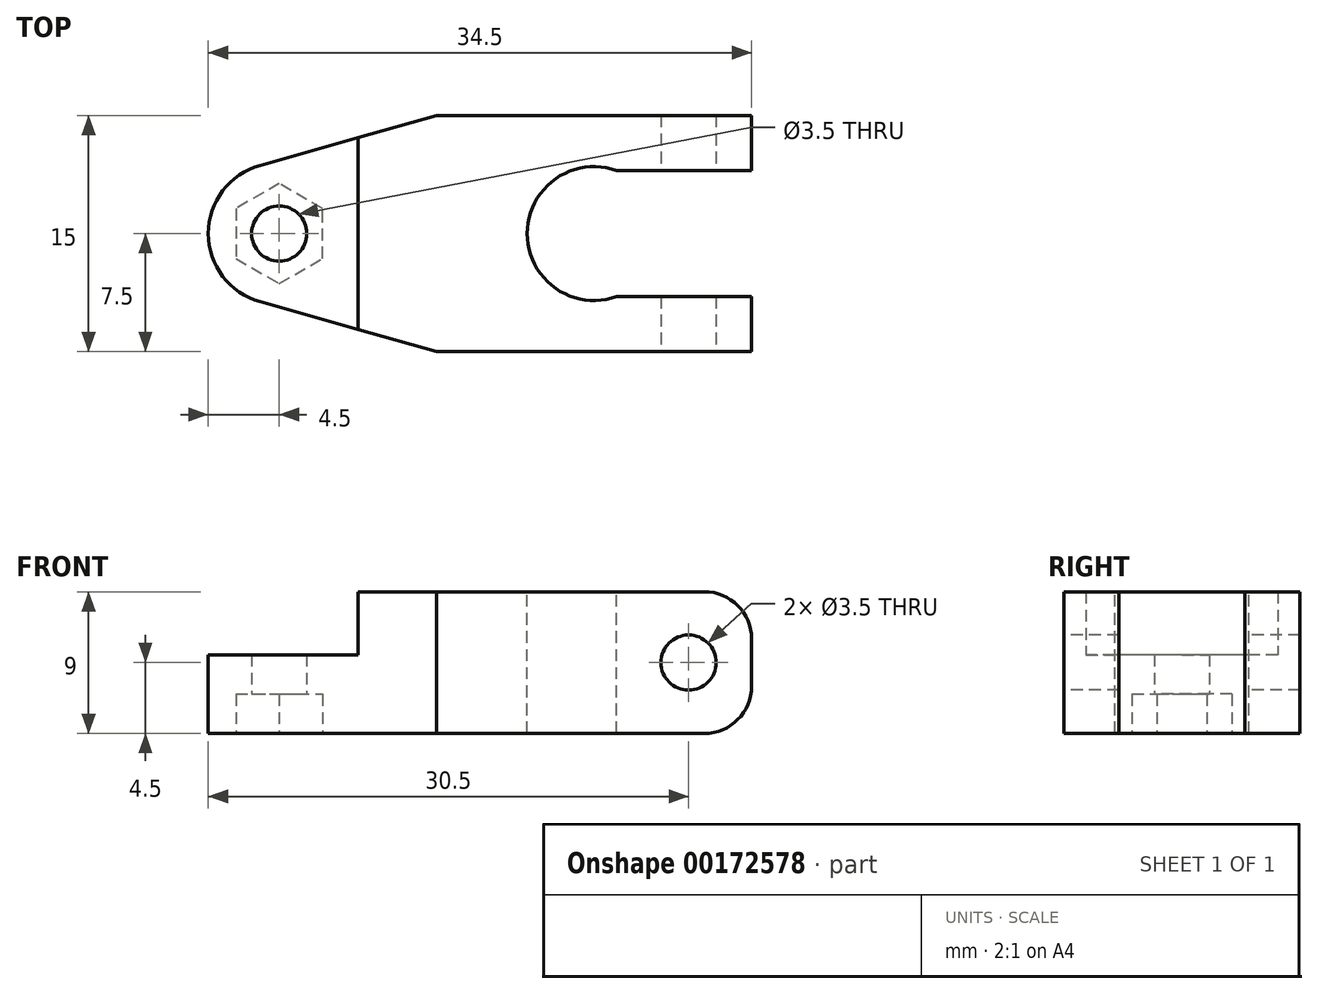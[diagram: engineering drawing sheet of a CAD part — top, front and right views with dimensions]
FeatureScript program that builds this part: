
annotation { "Feature Type Name" : "Feature", "Feature Type Description" : "" }
export const myFeature = defineFeature(function(context is Context, id is Id, definition is map)
    precondition{}
    {
        {
            var Q0;
            Q0=qCreatedBy(makeId("Top.planeOp"),FACE);
            var sketch = newSketch(context, id + "F0", { "sketchPlane" : qUnion([Q0])});
            skCircle(sketch, "E0", {"center": v(0, 0) * mm, "radius": 4.5 * mm});
            skCircle(sketch, "E1", {"center": v(0, 0) * mm, "radius": 1.75 * mm});
            skLineSegment(sketch, "E2.bottom", {"start": v(30, 7.5) * mm, "end": v(10, 7.5) * mm});
            skLineSegment(sketch, "E2.top", {"start": v(30, -7.5) * mm, "end": v(10, -7.5) * mm});
            skLineSegment(sketch, "E2.left", {"start": v(30, 7.5) * mm, "end": v(30, -7.5) * mm});
            skLineSegment(sketch, "E2.right", {"start": v(10, 7.5) * mm, "end": v(10, -7.5) * mm});
            skLineSegment(sketch, "E3", {"start": v(10, 7.5) * mm, "end": v(-1.22, 4.33) * mm});
            skLineSegment(sketch, "E4", {"start": v(10, -7.5) * mm, "end": v(-1.22, -4.33) * mm});
            skSolve(sketch);
        }
        {
            var Q0;
            Q0 = qSketchRegion(id + "F0", true);
            extrude(context, id + "F1", {"entities" : qUnion([Q0]), "depth" : 9 * mm, "offsetDistance" : 25 * mm});
        }
        {
            var Q0;
            Q0=makeQuery(id+"F1.opExtrude","CAP_FACE",FACE,{"disambiguationData":[OSD([sQuery(id+"F0.wireOp",EDGE,"E0"),sQuery(id+"F0.wireOp",EDGE,"M1rwKN8y-CayM-5D3e-yUcK-hpkHA81qaYvP.bottom"),sQuery(id+"F0.wireOp",EDGE,"M1rwKN8y-CayM-5D3e-yUcK-hpkHA81qaYvP.top"),sQuery(id+"F0.wireOp",EDGE,"M1rwKN8y-CayM-5D3e-yUcK-hpkHA81qaYvP.right"),sQuery(id+"F0.wireOp",EDGE,"E1")])],"isStart":false});
            var sketch = newSketch(context, id + "F2", { "sketchPlane" : qUnion([Q0])});
            skLineSegment(sketch, "E5.bottom", {"start": v(-7.93, 7.15) * mm, "end": v(5, 7.15) * mm});
            skLineSegment(sketch, "E5.top", {"start": v(-7.93, -8.4) * mm, "end": v(5, -8.4) * mm});
            skLineSegment(sketch, "E5.left", {"start": v(-7.93, 7.15) * mm, "end": v(-7.93, -8.4) * mm});
            skLineSegment(sketch, "E5.right", {"start": v(5, 7.15) * mm, "end": v(5, -8.4) * mm});
            skSolve(sketch);
        }
        {
            var Q0;
            Q0 = qSketchRegion(id + "F2", true);
            extrude(context, id + "F3", {"entities" : qUnion([Q0]), "operationType" : NewBodyOperationType.REMOVE, "oppositeDirection" : true, "depth" : 4 * mm, "offsetDistance" : 25 * mm});
        }
        {
            var Q0;
            Q0=makeQuery(id+"F1.opExtrude","CAP_FACE",FACE,{"disambiguationData":[OSD([sQuery(id+"F0.wireOp",EDGE,"E0"),sQuery(id+"F0.wireOp",EDGE,"M1rwKN8y-CayM-5D3e-yUcK-hpkHA81qaYvP.bottom"),sQuery(id+"F0.wireOp",EDGE,"M1rwKN8y-CayM-5D3e-yUcK-hpkHA81qaYvP.top"),sQuery(id+"F0.wireOp",EDGE,"M1rwKN8y-CayM-5D3e-yUcK-hpkHA81qaYvP.right"),sQuery(id+"F0.wireOp",EDGE,"E1")])],"isStart":true});
            var sketch = newSketch(context, id + "F4", { "sketchPlane" : qUnion([Q0])});
            skCircle(sketch, "E6.cCircle", {"center": v(0, 0) * mm, "radius": 2.75 * mm, "construction": true});
            skLineSegment(sketch, "E6.0", {"start": v(2.75, 1.59) * mm, "end": v(2.75, -1.59) * mm});
            skLineSegment(sketch, "E6.1", {"start": v(2.75, -1.59) * mm, "end": v(0, -3.18) * mm});
            skLineSegment(sketch, "E6.2", {"start": v(0, -3.18) * mm, "end": v(-2.75, -1.59) * mm});
            skLineSegment(sketch, "E6.3", {"start": v(-2.75, -1.59) * mm, "end": v(-2.75, 1.59) * mm});
            skLineSegment(sketch, "E6.4", {"start": v(-2.75, 1.59) * mm, "end": v(0, 3.18) * mm});
            skLineSegment(sketch, "E6.5", {"start": v(0, 3.18) * mm, "end": v(2.75, 1.59) * mm});
            skPoint(sketch, "E6.0.midPoint", {"position": v(2.75, 0) * mm});
            skSolve(sketch);
        }
        {
            var Q0;
            Q0 = qSketchRegion(id + "F4", true);
            extrude(context, id + "F5", {"entities" : qUnion([Q0]), "operationType" : NewBodyOperationType.REMOVE, "oppositeDirection" : true, "depth" : 2.5 * mm, "offsetDistance" : 25 * mm});
        }
        {
            var Q0;
            Q0=makeQuery(id+"F1.opExtrude","CAP_FACE",FACE,{"disambiguationData":[OSD([sQuery(id+"F0.wireOp",EDGE,"E0"),sQuery(id+"F0.wireOp",EDGE,"M1rwKN8y-CayM-5D3e-yUcK-hpkHA81qaYvP.bottom"),sQuery(id+"F0.wireOp",EDGE,"M1rwKN8y-CayM-5D3e-yUcK-hpkHA81qaYvP.top"),sQuery(id+"F0.wireOp",EDGE,"M1rwKN8y-CayM-5D3e-yUcK-hpkHA81qaYvP.right"),sQuery(id+"F0.wireOp",EDGE,"E1")])],"isStart":false});
            var sketch = newSketch(context, id + "F6", { "sketchPlane" : qUnion([Q0])});
            skCircle(sketch, "E7", {"center": v(20, 0) * mm, "radius": 4.25 * mm});
            skLineSegment(sketch, "E8.bottom", {"start": v(21.44, 4) * mm, "end": v(30, 4) * mm});
            skLineSegment(sketch, "E8.top", {"start": v(21.44, -4) * mm, "end": v(30, -4) * mm});
            skLineSegment(sketch, "E8.left", {"start": v(21.44, 4) * mm, "end": v(21.44, -4) * mm});
            skLineSegment(sketch, "E8.right", {"start": v(30, 4) * mm, "end": v(30, -4) * mm});
            skSolve(sketch);
        }
        {
            var Q0;
            Q0 = qSketchRegion(id + "F6", true);
            extrude(context, id + "F7", {"entities" : qUnion([Q0]), "operationType" : NewBodyOperationType.REMOVE, "oppositeDirection" : true, "depth" : 25 * mm, "offsetDistance" : 25 * mm});
        }
        {
            var Q0;
            Q0=makeQuery(id+"F1.opExtrude","SWEPT_FACE",FACE,{"disambiguationData":[OSD([sQuery(id+"F0.wireOp",EDGE,"E2.top")])]});
            var sketch = newSketch(context, id + "F8", { "sketchPlane" : qUnion([Q0])});
            skCircle(sketch, "E9", {"center": v(26, 4.5) * mm, "radius": 1.75 * mm});
            skPoint(sketch, "E9.centerSnap0", {"position": v(30, 4.5) * mm});
            skSolve(sketch);
        }
        {
            var Q0;
            Q0 = qSketchRegion(id + "F8", true);
            extrude(context, id + "F9", {"entities" : qUnion([Q0]), "operationType" : NewBodyOperationType.REMOVE, "oppositeDirection" : true, "depth" : 25 * mm, "offsetDistance" : 25 * mm});
        }
        {
            var Q0;
            {var subQ0=sQuery(id+"F0.wireOp",EDGE,"E2.left");var subQ1=sQuery(id+"F0.wireOp",EDGE,"E2.top");Q0=makeQuery(id+"F7.boolean.opBoolean","SPLIT",EDGE,{"disambiguationData":[TD([makeQuery(id+"F1.opExtrude","SWEPT_FACE",FACE,{"disambiguationData":[OSD([subQ1])]})])],"derivedFrom":makeQuery(id+"F1.opExtrude","CAP_EDGE",EDGE,{"disambiguationData":[OSD([subQ0])],"isStart":false})});}
            var Q1;
            {var subQ0=sQuery(id+"F0.wireOp",EDGE,"E2.left");var subQ1=sQuery(id+"F0.wireOp",EDGE,"E2.bottom");Q1=makeQuery(id+"F7.boolean.opBoolean","SPLIT",EDGE,{"disambiguationData":[TD([makeQuery(id+"F1.opExtrude","SWEPT_FACE",FACE,{"disambiguationData":[OSD([subQ1])]})])],"derivedFrom":makeQuery(id+"F1.opExtrude","CAP_EDGE",EDGE,{"disambiguationData":[OSD([subQ0])],"isStart":false})});}
            var Q2;
            {var subQ0=sQuery(id+"F0.wireOp",EDGE,"E2.left");var subQ1=sQuery(id+"F0.wireOp",EDGE,"E2.top");Q2=makeQuery(id+"F7.boolean.opBoolean","SPLIT",EDGE,{"disambiguationData":[TD([makeQuery(id+"F1.opExtrude","SWEPT_FACE",FACE,{"disambiguationData":[OSD([subQ1])]})])],"derivedFrom":makeQuery(id+"F1.opExtrude","CAP_EDGE",EDGE,{"disambiguationData":[OSD([subQ0])],"isStart":true})});}
            var Q3;
            {var subQ0=sQuery(id+"F0.wireOp",EDGE,"E2.left");var subQ1=sQuery(id+"F0.wireOp",EDGE,"E2.bottom");Q3=makeQuery(id+"F7.boolean.opBoolean","SPLIT",EDGE,{"disambiguationData":[TD([makeQuery(id+"F1.opExtrude","SWEPT_FACE",FACE,{"disambiguationData":[OSD([subQ1])]})])],"derivedFrom":makeQuery(id+"F1.opExtrude","CAP_EDGE",EDGE,{"disambiguationData":[OSD([subQ0])],"isStart":true})});}
            fillet(context, id + "F10", {"entities" : qUnion([Q0, Q1, Q2, Q3]), "radius" : 3 * mm, "tangentPropagation" : true, "allowEdgeOverflow" : false});
        }
    });
